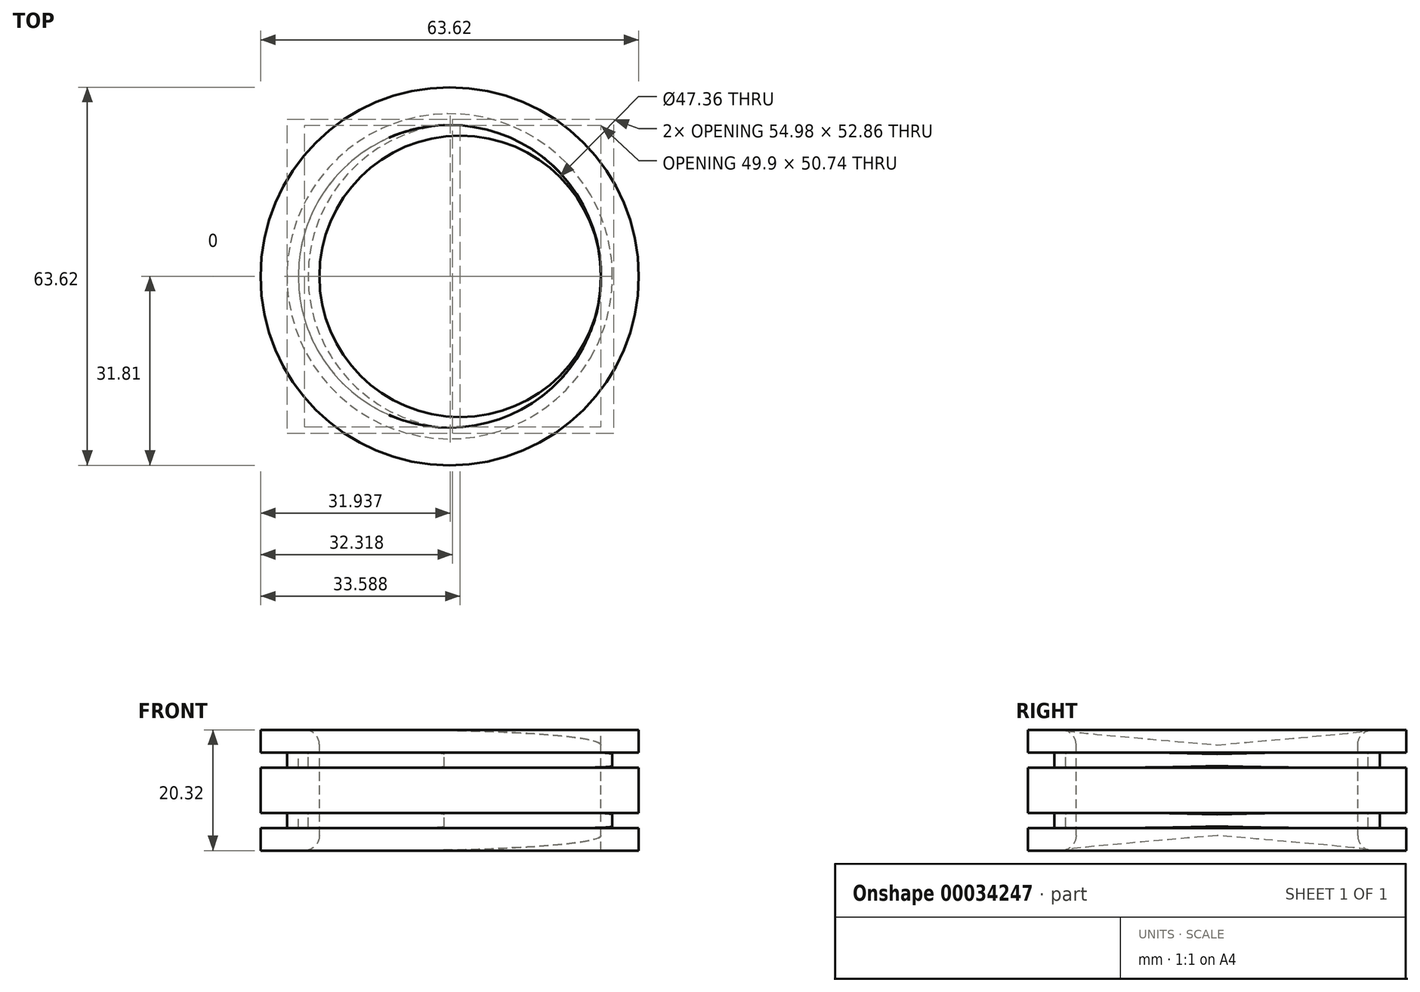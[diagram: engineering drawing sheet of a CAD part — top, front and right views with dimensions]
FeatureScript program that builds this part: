
annotation { "Feature Type Name" : "Feature", "Feature Type Description" : "" }
export const myFeature = defineFeature(function(context is Context, id is Id, definition is map)
    precondition{}
    {
        {
            var Q0;
            Q0=qCreatedBy(makeId("Front.planeOp"),FACE);
            var sketch = newSketch(context, id + "F0", { "sketchPlane" : qUnion([Q0])});
            skLineSegment(sketch, "E0.bottom", {"start": v(29.6, 30.06) * mm, "end": v(63.19, 30.06) * mm});
            skLineSegment(sketch, "E0.top", {"start": v(29.6, 4.66) * mm, "end": v(63.19, 4.66) * mm});
            skLineSegment(sketch, "E0.left", {"start": v(29.6, 30.06) * mm, "end": v(29.6, 4.66) * mm});
            skLineSegment(sketch, "E0.right", {"start": v(63.19, 30.06) * mm, "end": v(63.19, 4.66) * mm});
            skLineSegment(sketch, "E1.bottom", {"start": v(31.38, 27.52) * mm, "end": v(61.4, 27.52) * mm});
            skLineSegment(sketch, "E1.top", {"start": v(31.38, 7.2) * mm, "end": v(61.4, 7.2) * mm});
            skLineSegment(sketch, "E1.left", {"start": v(31.38, 27.52) * mm, "end": v(31.38, 7.2) * mm});
            skLineSegment(sketch, "E1.right", {"start": v(61.4, 27.52) * mm, "end": v(61.4, 7.2) * mm});
            skLineSegment(sketch, "E2", {"start": v(31.38, 27.52) * mm, "end": v(31.38, 30.06) * mm});
            skLineSegment(sketch, "E3", {"start": v(31.38, 30.06) * mm, "end": v(31.38, 7.2) * mm});
            skLineSegment(sketch, "E4", {"start": v(31.38, 7.2) * mm, "end": v(31.38, 4.66) * mm});
            skLineSegment(sketch, "E5", {"start": v(61.4, 30.06) * mm, "end": v(61.4, 4.66) * mm});
            skLineSegment(sketch, "E6.bottom", {"start": v(61.4, 23.71) * mm, "end": v(56.96, 23.71) * mm});
            skLineSegment(sketch, "E6.top", {"start": v(61.4, 21.17) * mm, "end": v(56.96, 21.17) * mm});
            skLineSegment(sketch, "E6.left", {"start": v(61.4, 23.71) * mm, "end": v(61.4, 21.17) * mm});
            skLineSegment(sketch, "E6.right", {"start": v(56.96, 23.71) * mm, "end": v(56.96, 21.17) * mm});
            skLineSegment(sketch, "E7.bottom", {"start": v(61.4, 13.55) * mm, "end": v(56.96, 13.55) * mm});
            skLineSegment(sketch, "E7.top", {"start": v(61.4, 11.01) * mm, "end": v(56.96, 11.01) * mm});
            skLineSegment(sketch, "E7.left", {"start": v(61.4, 13.55) * mm, "end": v(61.4, 11.01) * mm});
            skLineSegment(sketch, "E7.right", {"start": v(56.96, 13.55) * mm, "end": v(56.96, 11.01) * mm});
            skLineSegment(sketch, "E8", {"start": v(55.06, 27.52) * mm, "end": v(55.06, 7.2) * mm});
            skSolve(sketch);
        }
        {
            var Q0;
            {var subQ4=sQuery(id+"F0.wireOp",EDGE,"E6.bottom");Q0=makeQuery(id+"F0.imprint","IMPRINT",FACE,{"disambiguationData":[TD([[makeQuery(id+"F0.imprint","IMPRINT",EDGE,{"derivedFrom":subQ4}),-1.0]])]});}
            var Q1;
            Q1=sQuery(id+"F0.wireOp",EDGE,"E3");
            revolve(context, id + "F1", {"entities" : qUnion([Q0]), "axis" : qUnion([Q1]), "revolveType" : RevolveType.FULL});
        }
        {
            var Q0;
            Q0=makeQuery(id+"F1.opRevolve","SWEPT_EDGE",EDGE,{"disambiguationData":[OSD([sQuery(id+"F0.wireOp",EDGE,"E1.bottom"),sQuery(id+"F0.wireOp",EDGE,"E5")])]});
            var Q1;
            Q1=makeQuery(id+"F1.opRevolve","SWEPT_EDGE",EDGE,{"disambiguationData":[OSD([sQuery(id+"F0.wireOp",EDGE,"E1.bottom"),sQuery(id+"F0.wireOp",EDGE,"E8")])]});
            var Q2;
            Q2=makeQuery(id+"F1.opRevolve","SWEPT_EDGE",EDGE,{"disambiguationData":[OSD([sQuery(id+"F0.wireOp",EDGE,"E1.top"),sQuery(id+"F0.wireOp",EDGE,"E8")])]});
            var Q3;
            Q3=makeQuery(id+"F1.opRevolve","SWEPT_EDGE",EDGE,{"disambiguationData":[OSD([sQuery(id+"F0.wireOp",EDGE,"E1.top"),sQuery(id+"F0.wireOp",EDGE,"E5")])]});
            fillet(context, id + "F2", {"entities" : qUnion([Q0, Q1, Q2, Q3]), "radius" : 2.54 * mm, "tangentPropagation" : true, "allowEdgeOverflow" : false});
        }
        {
            var Q0;
            Q0=makeQuery(id+"F1.opRevolve","SWEPT_EDGE",EDGE,{"disambiguationData":[OSD([sQuery(id+"F0.wireOp",EDGE,"E5"),sQuery(id+"F0.wireOp",EDGE,"E6.top"),sQuery(id+"F0.wireOp",EDGE,"E6.left")])]});
            var Q1;
            Q1=makeQuery(id+"F1.opRevolve","SWEPT_EDGE",EDGE,{"disambiguationData":[OSD([sQuery(id+"F0.wireOp",EDGE,"E5"),sQuery(id+"F0.wireOp",EDGE,"E6.bottom"),sQuery(id+"F0.wireOp",EDGE,"E6.left")])]});
            var Q2;
            Q2=makeQuery(id+"F1.opRevolve","SWEPT_EDGE",EDGE,{"disambiguationData":[OSD([sQuery(id+"F0.wireOp",EDGE,"E5"),sQuery(id+"F0.wireOp",EDGE,"E7.bottom"),sQuery(id+"F0.wireOp",EDGE,"E7.left")])]});
            var Q3;
            Q3=makeQuery(id+"F1.opRevolve","SWEPT_EDGE",EDGE,{"disambiguationData":[OSD([sQuery(id+"F0.wireOp",EDGE,"E5"),sQuery(id+"F0.wireOp",EDGE,"E7.top"),sQuery(id+"F0.wireOp",EDGE,"E7.left")])]});
            fillet(context, id + "F3", {"entities" : qUnion([Q0, Q1, Q2, Q3]), "radius" : 0.25 * mm, "tangentPropagation" : true, "allowEdgeOverflow" : false});
        }
        {
            var Q0;
            {var subQ4=sQuery(id+"F0.wireOp",EDGE,"E6.bottom");Q0=makeQuery(id+"F0.imprint","IMPRINT",FACE,{"disambiguationData":[TD([[makeQuery(id+"F0.imprint","IMPRINT",EDGE,{"derivedFrom":subQ4}),-1.0]])]});}
            var Q1;
            Q1=sQuery(id+"F0.wireOp",EDGE,"E0.left");
            revolve(context, id + "F4", {"operationType" : NewBodyOperationType.ADD, "entities" : qUnion([Q0]), "axis" : qUnion([Q1]), "revolveType" : RevolveType.FULL});
        }
    });
